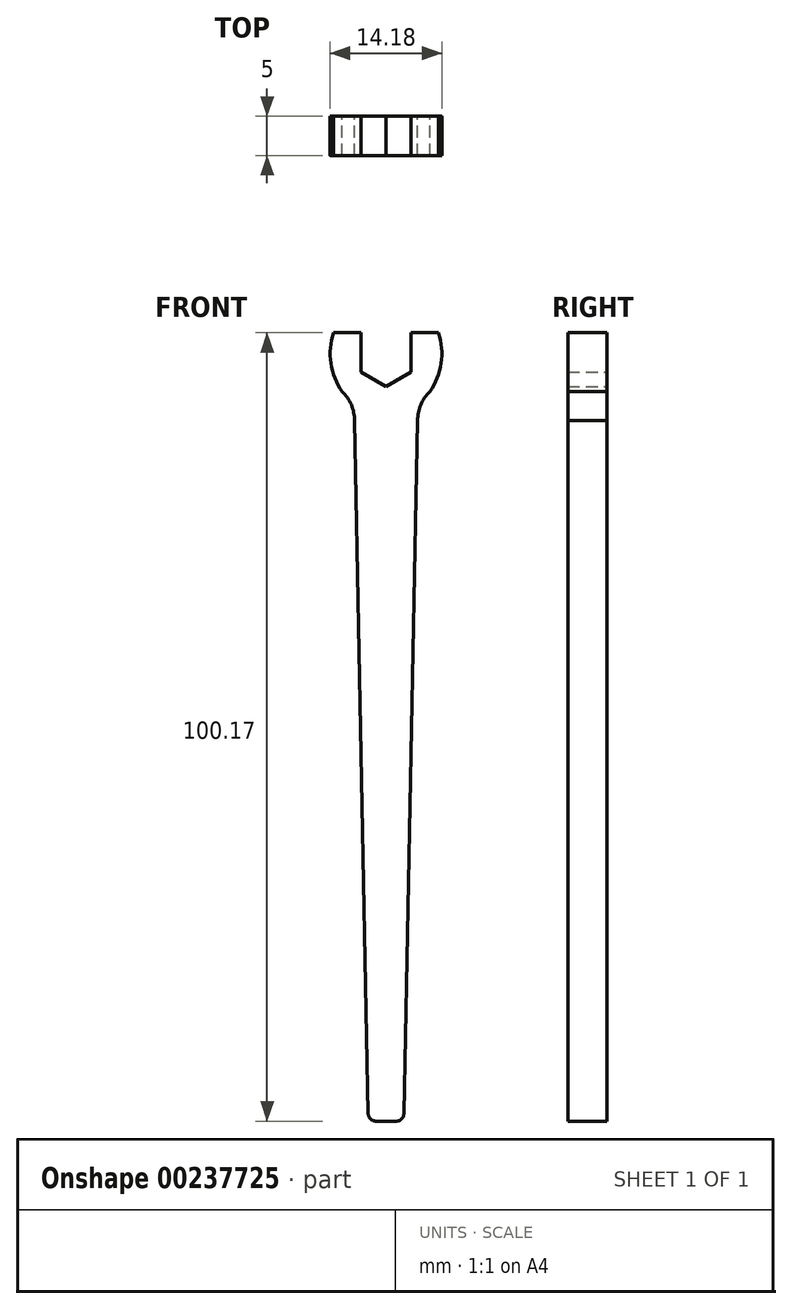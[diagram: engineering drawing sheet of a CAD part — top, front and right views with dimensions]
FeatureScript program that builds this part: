
annotation { "Feature Type Name" : "Feature", "Feature Type Description" : "" }
export const myFeature = defineFeature(function(context is Context, id is Id, definition is map)
    precondition{}
    {
        {
            var Q0;
            Q0=qCreatedBy(makeId("Front.planeOp"),FACE);
            var sketch = newSketch(context, id + "F0", { "sketchPlane" : qUnion([Q0])});
            skArc(sketch, "E0.cCircle", {"start": v(-3.17, 0) * mm, "mid": v(0, -3.17) * mm, "end": v(3.17, 0) * mm, "construction": true});
            skLineSegment(sketch, "E0.2", {"start": v(3.18, -1.83) * mm, "end": v(0, -3.67) * mm});
            skLineSegment(sketch, "E0.3", {"start": v(0, -3.67) * mm, "end": v(-3.17, -1.83) * mm});
            skPoint(sketch, "E1.orphan", {"position": v(0, 3.67) * mm});
            skCircle(sketch, "E2", {"center": v(0, 0) * mm, "radius": 9.5 * mm, "construction": true});
            skArc(sketch, "E3.filletArc", {"start": v(5.57, -4.32) * mm, "mid": v(4.4, -5.98) * mm, "end": v(4, -7.96) * mm});
            skArc(sketch, "E4.MirrorCS", {"start": v(-5.57, -4.32) * mm, "mid": v(-4.4, -5.98) * mm, "end": v(-4, -7.96) * mm});
            skLineSegment(sketch, "E5", {"start": v(3.18, -1.83) * mm, "end": v(3.18, 3.17) * mm});
            skLineSegment(sketch, "E6", {"start": v(3.17, 3.17) * mm, "end": v(6.68, 3.17) * mm});
            skArc(sketch, "E7", {"start": v(5.57, -4.32) * mm, "mid": v(7, -0.7) * mm, "end": v(6.67, 3.17) * mm});
            skArc(sketch, "E8.MirrorCS", {"start": v(-5.57, -4.32) * mm, "mid": v(-7, -0.7) * mm, "end": v(-6.67, 3.17) * mm});
            skLineSegment(sketch, "E9", {"start": v(-3.17, 3.17) * mm, "end": v(-3.17, -1.83) * mm});
            skLineSegment(sketch, "E10", {"start": v(-6.67, 3.17) * mm, "end": v(-3.17, 3.17) * mm});
            skLineSegment(sketch, "E11", {"start": v(4, -7.96) * mm, "end": v(2.27, -96.02) * mm});
            skLineSegment(sketch, "E12.MirrorCS", {"start": v(-4, -7.96) * mm, "end": v(-2.27, -96.02) * mm});
            skLineSegment(sketch, "E13", {"start": v(-1.27, -97) * mm, "end": v(1.27, -97) * mm});
            skPoint(sketch, "E14.visualSharp", {"position": v(-2.25, -97) * mm});
            skArc(sketch, "E14.filletArc", {"start": v(-2.27, -96.02) * mm, "mid": v(-1.97, -96.71) * mm, "end": v(-1.27, -97) * mm});
            skPoint(sketch, "E15.visualSharp", {"position": v(2.25, -97) * mm});
            skArc(sketch, "E15.filletArc", {"start": v(1.27, -97) * mm, "mid": v(1.97, -96.71) * mm, "end": v(2.27, -96.02) * mm});
            skSolve(sketch);
        }
        {
            var Q0;
            Q0=makeQuery(id+"F0.imprint","IMPRINT",FACE,{"disambiguationData":[TD([[makeQuery(id+"F0.imprint","IMPRINT",EDGE,{"derivedFrom":sQuery(id+"F0.wireOp",EDGE,"E0.2")}),1.0]])]});
            extrude(context, id + "F1", {"entities" : qUnion([Q0]), "depth" : 5 * mm});
        }
    });
